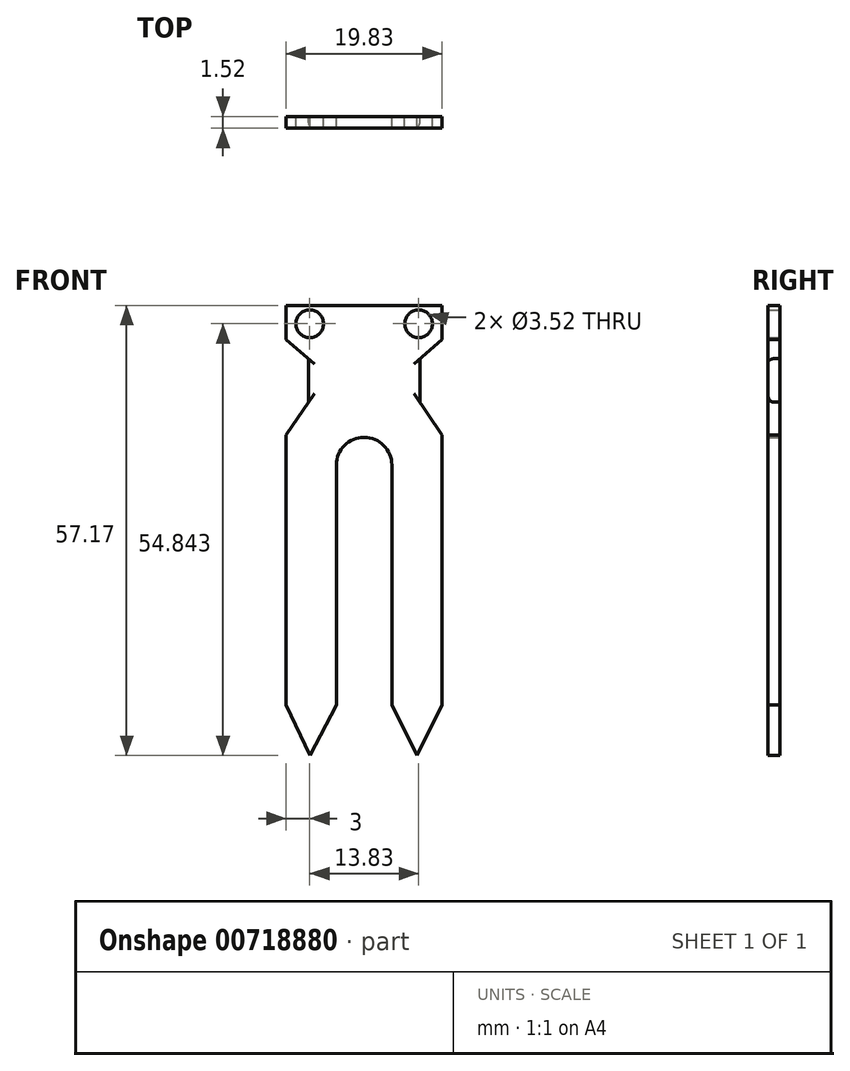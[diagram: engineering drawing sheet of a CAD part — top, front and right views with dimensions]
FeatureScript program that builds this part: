
annotation { "Feature Type Name" : "Feature", "Feature Type Description" : "" }
export const myFeature = defineFeature(function(context is Context, id is Id, definition is map)
    precondition{}
    {
        {
            var Q0;
            Q0=qCreatedBy(makeId("Front.planeOp"),FACE);
            var sketch = newSketch(context, id + "F0", { "sketchPlane" : qUnion([Q0])});
            skLineSegment(sketch, "E0.bottom", {"start": v(-19.83, 42.28) * mm, "end": v(-13.44, 42.28) * mm});
            skLineSegment(sketch, "E0.top", {"start": v(-19.83, -8.47) * mm, "end": v(-13.44, -8.47) * mm});
            skLineSegment(sketch, "E0.left", {"start": v(-19.83, 42.28) * mm, "end": v(-19.83, 38.15) * mm});
            skLineSegment(sketch, "E0.right", {"start": v(-13.44, 42.28) * mm, "end": v(-13.44, -8.47) * mm});
            skLineSegment(sketch, "E1.bottom", {"start": v(-6.4, 42.28) * mm, "end": v(0, 42.28) * mm});
            skLineSegment(sketch, "E1.top", {"start": v(-6.39, -8.47) * mm, "end": v(0, -8.47) * mm});
            skLineSegment(sketch, "E1.left", {"start": v(-6.4, 42.28) * mm, "end": v(-6.39, -8.47) * mm});
            skLineSegment(sketch, "E1.right", {"start": v(0, 42.28) * mm, "end": v(0, 37.96) * mm});
            skLineSegment(sketch, "E2", {"start": v(-19.83, 42.28) * mm, "end": v(0, 42.28) * mm});
            skLineSegment(sketch, "E3.left", {"start": v(-19.83, 42.28) * mm, "end": v(-19.83, 41.23) * mm});
            skLineSegment(sketch, "E3.right", {"start": v(0, 42.28) * mm, "end": v(0, 41.23) * mm});
            skLineSegment(sketch, "E4", {"start": v(-19.83, -8.47) * mm, "end": v(-16.77, -14.89) * mm});
            skLineSegment(sketch, "E5", {"start": v(-16.77, -14.89) * mm, "end": v(-13.44, -8.47) * mm});
            skLineSegment(sketch, "E6", {"start": v(-6.39, -8.47) * mm, "end": v(-3.2, -14.89) * mm});
            skPoint(sketch, "E6.endSnap0", {"position": v(-3.2, -8.47) * mm});
            skLineSegment(sketch, "E7", {"start": v(-3.2, -14.89) * mm, "end": v(0, -8.47) * mm});
            skPoint(sketch, "E8.snap10", {"position": v(-9.92, 22) * mm});
            skLineSegment(sketch, "E9.bottom", {"start": v(-13.44, 42.28) * mm, "end": v(-6.39, 42.28) * mm});
            skLineSegment(sketch, "E9.left", {"start": v(-13.44, 42.28) * mm, "end": v(-13.44, 22) * mm});
            skLineSegment(sketch, "E10", {"start": v(-13.44, 22) * mm, "end": v(-13.44, 42.28) * mm});
            skLineSegment(sketch, "E11", {"start": v(-13.44, 42.28) * mm, "end": v(-6.4, 42.28) * mm});
            skLineSegment(sketch, "E12", {"start": v(-6.39, 42.28) * mm, "end": v(-6.39, 23.08) * mm});
            skArc(sketch, "E13", {"start": v(-6.4, 22) * mm, "mid": v(-9.91, 25.53) * mm, "end": v(-13.44, 22) * mm});
            skLineSegment(sketch, "E14", {"start": v(-9.91, 25.53) * mm, "end": v(-9.92, 42.28) * mm});
            skCircle(sketch, "E15", {"center": v(-3, 39.95) * mm, "radius": 1.76 * mm});
            skCircle(sketch, "E16", {"center": v(-16.83, 39.95) * mm, "radius": 1.76 * mm});
            skLineSegment(sketch, "E17", {"start": v(0, 37.96) * mm, "end": v(-2.84, 35.51) * mm});
            skLineSegment(sketch, "E18", {"start": v(-2.84, 35.51) * mm, "end": v(-2.84, 29.98) * mm});
            skLineSegment(sketch, "E19", {"start": v(-2.84, 29.98) * mm, "end": v(0, 25.85) * mm});
            skLineSegment(sketch, "E20.trimOffspring", {"start": v(0, 25.85) * mm, "end": v(0, -8.47) * mm});
            skLineSegment(sketch, "E21.trimOffspring", {"start": v(0, 25.85) * mm, "end": v(0, 25.43) * mm});
            skLineSegment(sketch, "E22.trimOffspring", {"start": v(-19.83, 26.04) * mm, "end": v(-19.83, 25.43) * mm});
            skLineSegment(sketch, "E23.trimOffspring", {"start": v(-19.83, 26.04) * mm, "end": v(-19.83, -8.47) * mm});
            skLineSegment(sketch, "E24.MirrorCS", {"start": v(-19.83, 37.96) * mm, "end": v(-17, 35.51) * mm});
            skLineSegment(sketch, "E25.MirrorCS", {"start": v(-17, 35.51) * mm, "end": v(-17, 29.98) * mm});
            skLineSegment(sketch, "E26.MirrorCS", {"start": v(-17, 29.98) * mm, "end": v(-19.83, 25.85) * mm});
            skLineSegment(sketch, "E27.top", {"start": v(-19.83, 22) * mm, "end": v(-13.44, 22) * mm});
            skLineSegment(sketch, "E27.left", {"start": v(-19.83, -8.47) * mm, "end": v(-19.83, 22) * mm});
            skLineSegment(sketch, "E27.right", {"start": v(-13.44, -8.47) * mm, "end": v(-13.44, 22) * mm});
            skLineSegment(sketch, "E28.left", {"start": v(-19.83, 42.28) * mm, "end": v(-19.83, 37.96) * mm});
            skLineSegment(sketch, "E29.trimOffspring", {"start": v(-19.83, 26.04) * mm, "end": v(-19.83, 22) * mm});
            skSolve(sketch);
        }
        {
            var Q0;
            Q0 = qSketchRegion(id + "F0", true);
            extrude(context, id + "F1", {"entities" : qUnion([Q0]), "depth" : 1.52 * mm, "offsetDistance" : 25 * mm});
        }
        {
            var Q0;
            Q0=makeQuery(id+"F1.opExtrude","CAP_EDGE",EDGE,{"disambiguationData":[OSD([sQuery(id+"F0.wireOp",EDGE,"E25.MirrorCS")])],"isStart":false});
            var Q1;
            Q1=makeQuery(id+"F1.opExtrude","CAP_EDGE",EDGE,{"disambiguationData":[OSD([sQuery(id+"F0.wireOp",EDGE,"E18")])],"isStart":false});
            fillet(context, id + "F2", {"entities" : qUnion([Q0, Q1]), "radius" : .75 * mm, "tangentPropagation" : true, "allowEdgeOverflow" : false});
        }
    });
